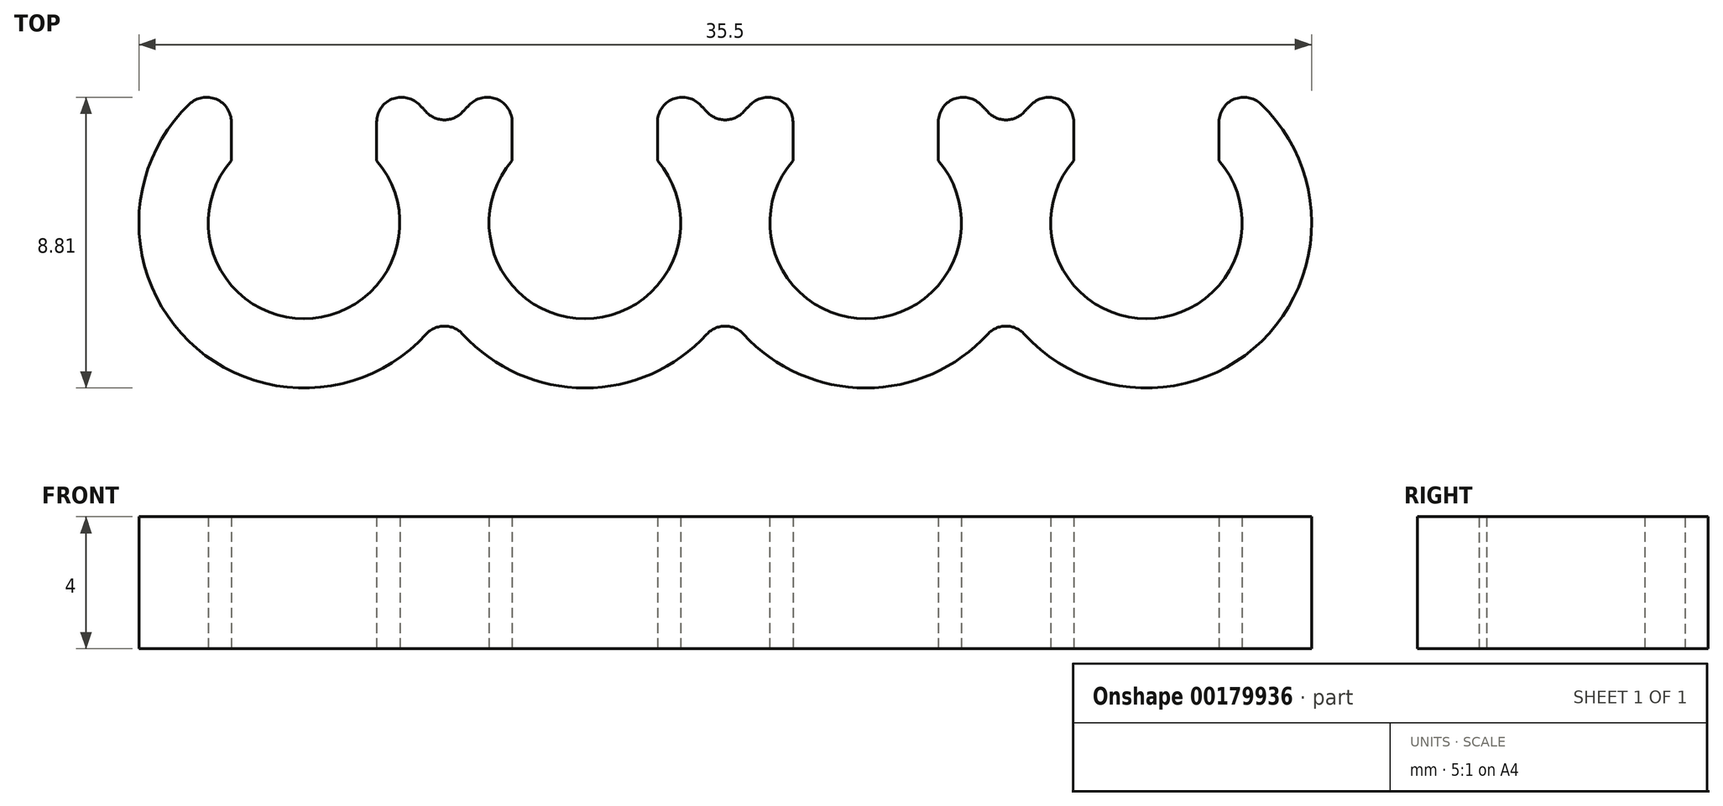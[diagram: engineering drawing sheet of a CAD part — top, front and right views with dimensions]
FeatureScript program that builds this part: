
annotation { "Feature Type Name" : "Feature", "Feature Type Description" : "" }
export const myFeature = defineFeature(function(context is Context, id is Id, definition is map)
    precondition{}
    {
        {
            var Q0;
            Q0=qCreatedBy(makeId("Top.planeOp"),FACE);
            var sketch = newSketch(context, id + "F0", { "sketchPlane" : qUnion([Q0])});
            skArc(sketch, "E0", {"start": v(-2.2, 1.89) * mm, "mid": v(0, -2.9) * mm, "end": v(2.2, 1.89) * mm});
            skArc(sketch, "E1", {"start": v(-2.2, 4.49) * mm, "mid": v(0, -5) * mm, "end": v(2.2, 4.49) * mm});
            skLineSegment(sketch, "E2.left", {"start": v(2.2, 4.49) * mm, "end": v(2.2, 1.89) * mm});
            skLineSegment(sketch, "E2.right", {"start": v(-2.2, 4.49) * mm, "end": v(-2.2, 1.89) * mm});
            skArc(sketch, "E3.1.0.0", {"start": v(6.3, 4.49) * mm, "mid": v(8.5, -5) * mm, "end": v(10.7, 4.49) * mm});
            skArc(sketch, "E3.1.0.1", {"start": v(6.3, 1.89) * mm, "mid": v(8.5, -2.9) * mm, "end": v(10.7, 1.89) * mm});
            skLineSegment(sketch, "E3.1.0.2", {"start": v(10.7, 4.49) * mm, "end": v(10.7, 1.89) * mm});
            skLineSegment(sketch, "E3.1.0.3", {"start": v(6.3, 4.49) * mm, "end": v(6.3, 1.89) * mm});
            skArc(sketch, "E3.2.0.0", {"start": v(14.8, 4.49) * mm, "mid": v(17, -5) * mm, "end": v(19.2, 4.49) * mm});
            skArc(sketch, "E3.2.0.1", {"start": v(14.8, 1.89) * mm, "mid": v(17, -2.9) * mm, "end": v(19.2, 1.89) * mm});
            skLineSegment(sketch, "E3.2.0.2", {"start": v(19.2, 4.49) * mm, "end": v(19.2, 1.89) * mm});
            skLineSegment(sketch, "E3.2.0.3", {"start": v(14.8, 4.49) * mm, "end": v(14.8, 1.89) * mm});
            skArc(sketch, "E3.3.0.0", {"start": v(23.3, 4.49) * mm, "mid": v(25.5, -5) * mm, "end": v(27.7, 4.49) * mm});
            skArc(sketch, "E3.3.0.1", {"start": v(23.3, 1.89) * mm, "mid": v(25.5, -2.9) * mm, "end": v(27.7, 1.89) * mm});
            skLineSegment(sketch, "E3.3.0.2", {"start": v(27.7, 4.49) * mm, "end": v(27.7, 1.89) * mm});
            skLineSegment(sketch, "E3.3.0.3", {"start": v(23.3, 4.49) * mm, "end": v(23.3, 1.89) * mm});
            skLineSegment(sketch, "E3.direction1", {"start": v(0, 0) * mm, "end": v(8.5, 0) * mm, "construction": true});
            skSolve(sketch);
        }
        {
            var Q0;
            Q0 = qSketchRegion(id + "F0", true);
            extrude(context, id + "F1", {"entities" : qUnion([Q0]), "depth" : 4 * mm});
        }
        {
            var Q0;
            Q0=makeQuery(id+"F1.opExtrude","SWEPT_EDGE",EDGE,{"disambiguationData":[OSD([sQuery(id+"F0.wireOp",EDGE,"E1"),sQuery(id+"F0.wireOp",EDGE,"E2.right")])]});
            var Q1;
            Q1=makeQuery(id+"F1.opExtrude","SWEPT_EDGE",EDGE,{"disambiguationData":[OSD([sQuery(id+"F0.wireOp",EDGE,"E1"),sQuery(id+"F0.wireOp",EDGE,"E2.left")])]});
            var Q2;
            Q2=makeQuery(id+"F1.opExtrude","SWEPT_EDGE",EDGE,{"disambiguationData":[OSD([sQuery(id+"F0.wireOp",EDGE,"E3.1.0.0"),sQuery(id+"F0.wireOp",EDGE,"E3.1.0.3")])]});
            var Q3;
            Q3=makeQuery(id+"F1.opExtrude","SWEPT_EDGE",EDGE,{"disambiguationData":[OSD([sQuery(id+"F0.wireOp",EDGE,"E3.1.0.0"),sQuery(id+"F0.wireOp",EDGE,"E3.1.0.2")])]});
            var Q4;
            Q4=makeQuery(id+"F1.opExtrude","SWEPT_EDGE",EDGE,{"disambiguationData":[OSD([sQuery(id+"F0.wireOp",EDGE,"E3.2.0.0"),sQuery(id+"F0.wireOp",EDGE,"E3.2.0.3")])]});
            var Q5;
            Q5=makeQuery(id+"F1.opExtrude","SWEPT_EDGE",EDGE,{"disambiguationData":[OSD([sQuery(id+"F0.wireOp",EDGE,"E3.2.0.0"),sQuery(id+"F0.wireOp",EDGE,"E3.2.0.2")])]});
            var Q6;
            Q6=makeQuery(id+"F1.opExtrude","SWEPT_EDGE",EDGE,{"disambiguationData":[OSD([sQuery(id+"F0.wireOp",EDGE,"E3.3.0.0"),sQuery(id+"F0.wireOp",EDGE,"E3.3.0.3")])]});
            var Q7;
            Q7=makeQuery(id+"F1.opExtrude","SWEPT_EDGE",EDGE,{"disambiguationData":[OSD([sQuery(id+"F0.wireOp",EDGE,"E3.3.0.0"),sQuery(id+"F0.wireOp",EDGE,"E3.3.0.2")])]});
            var Q8;
            {var subQ0=sQuery(id+"F0.wireOp",EDGE,"E3.3.0.0");var subQ1=sQuery(id+"F0.wireOp",EDGE,"E3.2.0.0");Q8=makeQuery(id+"F1.opExtrude","SWEPT_EDGE",EDGE,{"disambiguationData":[OSD([subQ1,subQ0]),TDD([makeQuery(id+"F0.imprint","INTERSECT",VERTEX,{"disambiguationData":[OD(1.0)],"derivedFrom":[subQ1,subQ0]})])]});}
            var Q9;
            {var subQ0=sQuery(id+"F0.wireOp",EDGE,"E3.2.0.0");var subQ1=sQuery(id+"F0.wireOp",EDGE,"E3.1.0.0");Q9=makeQuery(id+"F1.opExtrude","SWEPT_EDGE",EDGE,{"disambiguationData":[OSD([subQ1,subQ0]),TDD([makeQuery(id+"F0.imprint","INTERSECT",VERTEX,{"disambiguationData":[OD(1.0)],"derivedFrom":[subQ1,subQ0]})])]});}
            var Q10;
            {var subQ0=sQuery(id+"F0.wireOp",EDGE,"E3.1.0.0");var subQ1=sQuery(id+"F0.wireOp",EDGE,"E1");Q10=makeQuery(id+"F1.opExtrude","SWEPT_EDGE",EDGE,{"disambiguationData":[OSD([subQ1,subQ0]),TDD([makeQuery(id+"F0.imprint","INTERSECT",VERTEX,{"disambiguationData":[OD(1.0)],"derivedFrom":[subQ1,subQ0]})])]});}
            var Q11;
            {var subQ0=sQuery(id+"F0.wireOp",EDGE,"E3.3.0.0");var subQ1=sQuery(id+"F0.wireOp",EDGE,"E3.2.0.0");Q11=makeQuery(id+"F1.opExtrude","SWEPT_EDGE",EDGE,{"disambiguationData":[OSD([subQ1,subQ0]),TDD([makeQuery(id+"F0.imprint","INTERSECT",VERTEX,{"disambiguationData":[OD(0.0)],"derivedFrom":[subQ1,subQ0]})])]});}
            var Q12;
            {var subQ0=sQuery(id+"F0.wireOp",EDGE,"E3.2.0.0");var subQ1=sQuery(id+"F0.wireOp",EDGE,"E3.1.0.0");Q12=makeQuery(id+"F1.opExtrude","SWEPT_EDGE",EDGE,{"disambiguationData":[OSD([subQ1,subQ0]),TDD([makeQuery(id+"F0.imprint","INTERSECT",VERTEX,{"disambiguationData":[OD(0.0)],"derivedFrom":[subQ1,subQ0]})])]});}
            var Q13;
            {var subQ0=sQuery(id+"F0.wireOp",EDGE,"E3.1.0.0");var subQ1=sQuery(id+"F0.wireOp",EDGE,"E1");Q13=makeQuery(id+"F1.opExtrude","SWEPT_EDGE",EDGE,{"disambiguationData":[OSD([subQ1,subQ0]),TDD([makeQuery(id+"F0.imprint","INTERSECT",VERTEX,{"disambiguationData":[OD(0.0)],"derivedFrom":[subQ1,subQ0]})])]});}
            fillet(context, id + "F2", {"entities" : qUnion([Q0, Q1, Q2, Q3, Q4, Q5, Q6, Q7, Q8, Q9, Q10, Q11, Q12, Q13]), "radius" : 0.75 * mm, "tangentPropagation" : true, "allowEdgeOverflow" : false});
        }
    });
